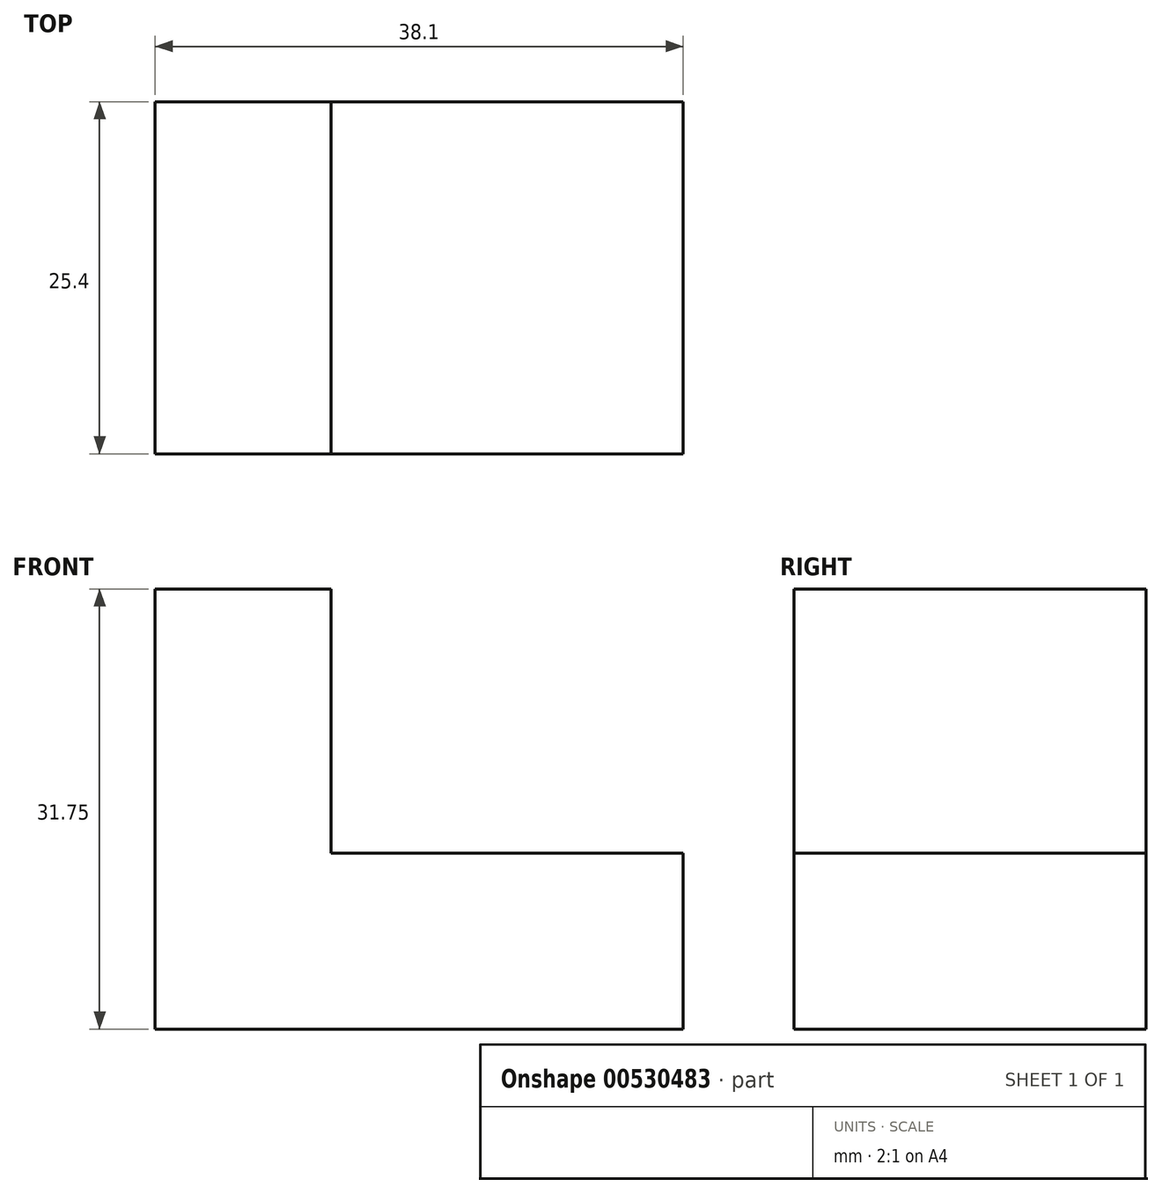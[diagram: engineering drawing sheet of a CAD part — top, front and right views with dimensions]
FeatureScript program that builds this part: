
annotation { "Feature Type Name" : "Feature", "Feature Type Description" : "" }
export const myFeature = defineFeature(function(context is Context, id is Id, definition is map)
    precondition{}
    {
        {
            var Q0;
            Q0=qCreatedBy(makeId("Front.planeOp"),FACE);
            var sketch = newSketch(context, id + "F0", { "sketchPlane" : qUnion([Q0])});
            skLineSegment(sketch, "E0", {"start": v(-44.17, 31.75) * mm, "end": v(-44.17, 0) * mm});
            skLineSegment(sketch, "E1", {"start": v(-44.17, 31.75) * mm, "end": v(-31.47, 31.75) * mm});
            skLineSegment(sketch, "E2", {"start": v(-31.47, 12.7) * mm, "end": v(-6.07, 12.7) * mm});
            skLineSegment(sketch, "E3", {"start": v(-44.17, 0) * mm, "end": v(-6.07, 0) * mm});
            skLineSegment(sketch, "E4", {"start": v(-31.47, 31.75) * mm, "end": v(-31.47, 12.7) * mm});
            skLineSegment(sketch, "E5", {"start": v(-6.07, 12.7) * mm, "end": v(-6.07, 0) * mm});
            skSolve(sketch);
        }
        {
            var Q0;
            Q0 = qSketchRegion(id + "F0", true);
            extrude(context, id + "F1", {"entities" : qUnion([Q0]), "depth" : 25.4 * mm, "offsetDistance" : 25.4 * mm});
        }
    });
